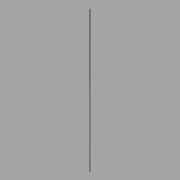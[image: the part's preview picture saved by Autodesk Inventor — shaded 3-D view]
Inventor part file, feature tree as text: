
AUTODESK INVENTOR PART (.ipt)
format: ipt  version: 2014 (Build 180170000, 170)  size: 64,000 bytes
history: native  units: mm
features: extrude x1, sketch x1
ambient origin geometry x8: Origin, YZ Plane, XZ Plane, XY Plane, X Axis, Y Axis, Z Axis, Center Point
bodies: Solid1 (feature_tree)
feature tree (2):
  extrude  "Extrusion1"  Depth=2600.0mm
  sketch  "Sketch1"  dims[d0=26.0mm d1=24.0mm d2=2600.0mm d3=0.0mm]
